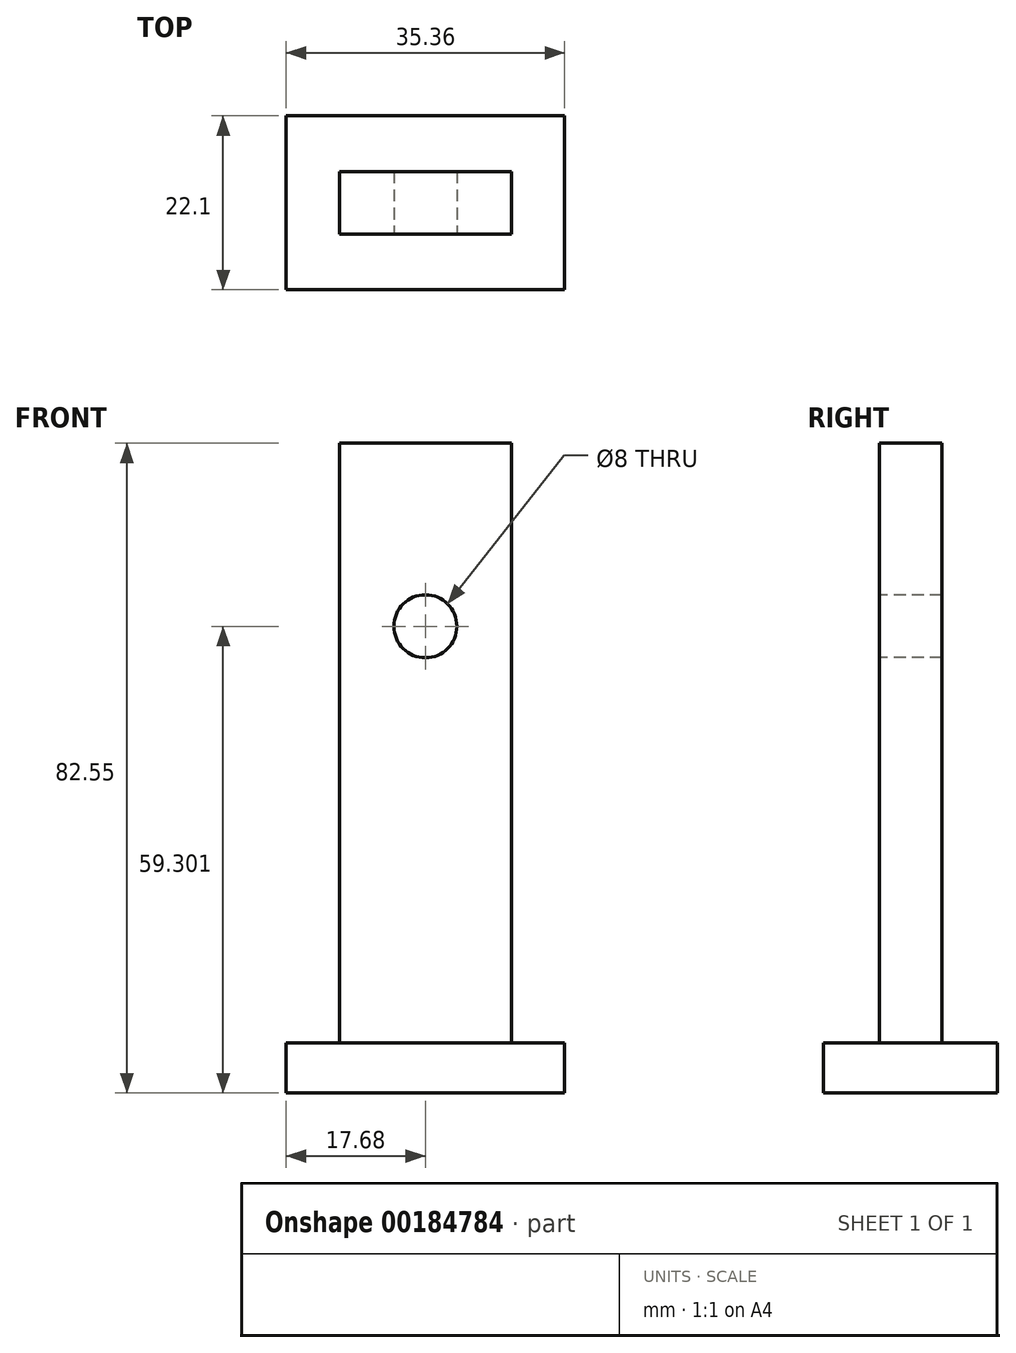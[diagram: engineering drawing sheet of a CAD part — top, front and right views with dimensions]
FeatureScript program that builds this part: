
annotation { "Feature Type Name" : "Feature", "Feature Type Description" : "" }
export const myFeature = defineFeature(function(context is Context, id is Id, definition is map)
    precondition{}
    {
        {
            var Q0;
            Q0=qCreatedBy(makeId("Top.planeOp"),FACE);
            var sketch = newSketch(context, id + "F0", { "sketchPlane" : qUnion([Q0])});
            skLineSegment(sketch, "E0.bottom", {"start": v(17.68, 11.05) * mm, "end": v(-17.68, 11.05) * mm});
            skLineSegment(sketch, "E0.top", {"start": v(17.68, -11.05) * mm, "end": v(-17.68, -11.05) * mm});
            skLineSegment(sketch, "E0.left", {"start": v(17.68, 11.05) * mm, "end": v(17.68, -11.05) * mm});
            skLineSegment(sketch, "E0.right", {"start": v(-17.68, 11.05) * mm, "end": v(-17.68, -11.05) * mm});
            skPoint(sketch, "E0.middle", {"position": v(0, 0) * mm});
            skSolve(sketch);
        }
        {
            var Q0;
            Q0=makeQuery(id+"F0.imprint","IMPRINT",FACE,{"disambiguationData":[TD([[makeQuery(id+"F0.imprint","IMPRINT",EDGE,{"derivedFrom":sQuery(id+"F0.wireOp",EDGE,"E0.bottom")}),1.0]])]});
            extrude(context, id + "F1", {"entities" : qUnion([Q0]), "depth" : 6.35 * mm});
        }
        {
            var Q0;
            Q0=makeQuery(id+"F1.opExtrude","CAP_FACE",FACE,{"disambiguationData":[OSD([sQuery(id+"F0.wireOp",EDGE,"E0.bottom"),sQuery(id+"F0.wireOp",EDGE,"E0.top"),sQuery(id+"F0.wireOp",EDGE,"E0.left"),sQuery(id+"F0.wireOp",EDGE,"E0.right")])],"isStart":false});
            var sketch = newSketch(context, id + "F2", { "sketchPlane" : qUnion([Q0])});
            skLineSegment(sketch, "E1.bottom", {"start": v(10.9, 3.98) * mm, "end": v(-10.9, 3.98) * mm});
            skLineSegment(sketch, "E1.top", {"start": v(10.9, -3.98) * mm, "end": v(-10.9, -3.98) * mm});
            skLineSegment(sketch, "E1.left", {"start": v(10.9, 3.98) * mm, "end": v(10.9, -3.98) * mm});
            skLineSegment(sketch, "E1.right", {"start": v(-10.9, 3.98) * mm, "end": v(-10.9, -3.98) * mm});
            skPoint(sketch, "E1.middle", {"position": v(0, 0) * mm});
            skSolve(sketch);
        }
        {
            var Q0;
            Q0=qSketchRegion(id+"F2",true);
            extrude(context, id + "F3", {"entities" : qUnion([Q0]), "depth" : 76.2 * mm});
        }
        {
            var Q0;
            Q0=makeQuery(id+"F3.opExtrude","SWEPT_FACE",FACE,{"disambiguationData":[OSD([sQuery(id+"F2.wireOp",EDGE,"E1.top")])]});
            var sketch = newSketch(context, id + "F4", { "sketchPlane" : qUnion([Q0])});
            skCircle(sketch, "E2", {"center": v(0, 59.3) * mm, "radius": 4 * mm});
            skPoint(sketch, "E3", {"position": v(0, 82.55) * mm});
            skSolve(sketch);
        }
        {
            var Q0;
            Q0=qSketchRegion(id+"F4",true);
            extrude(context, id + "F5", {"entities" : qUnion([Q0]), "operationType" : NewBodyOperationType.REMOVE, "endBound" : BoundingType.THROUGH_ALL, "oppositeDirection" : true, "depth" : 25.4 * mm});
        }
    });
